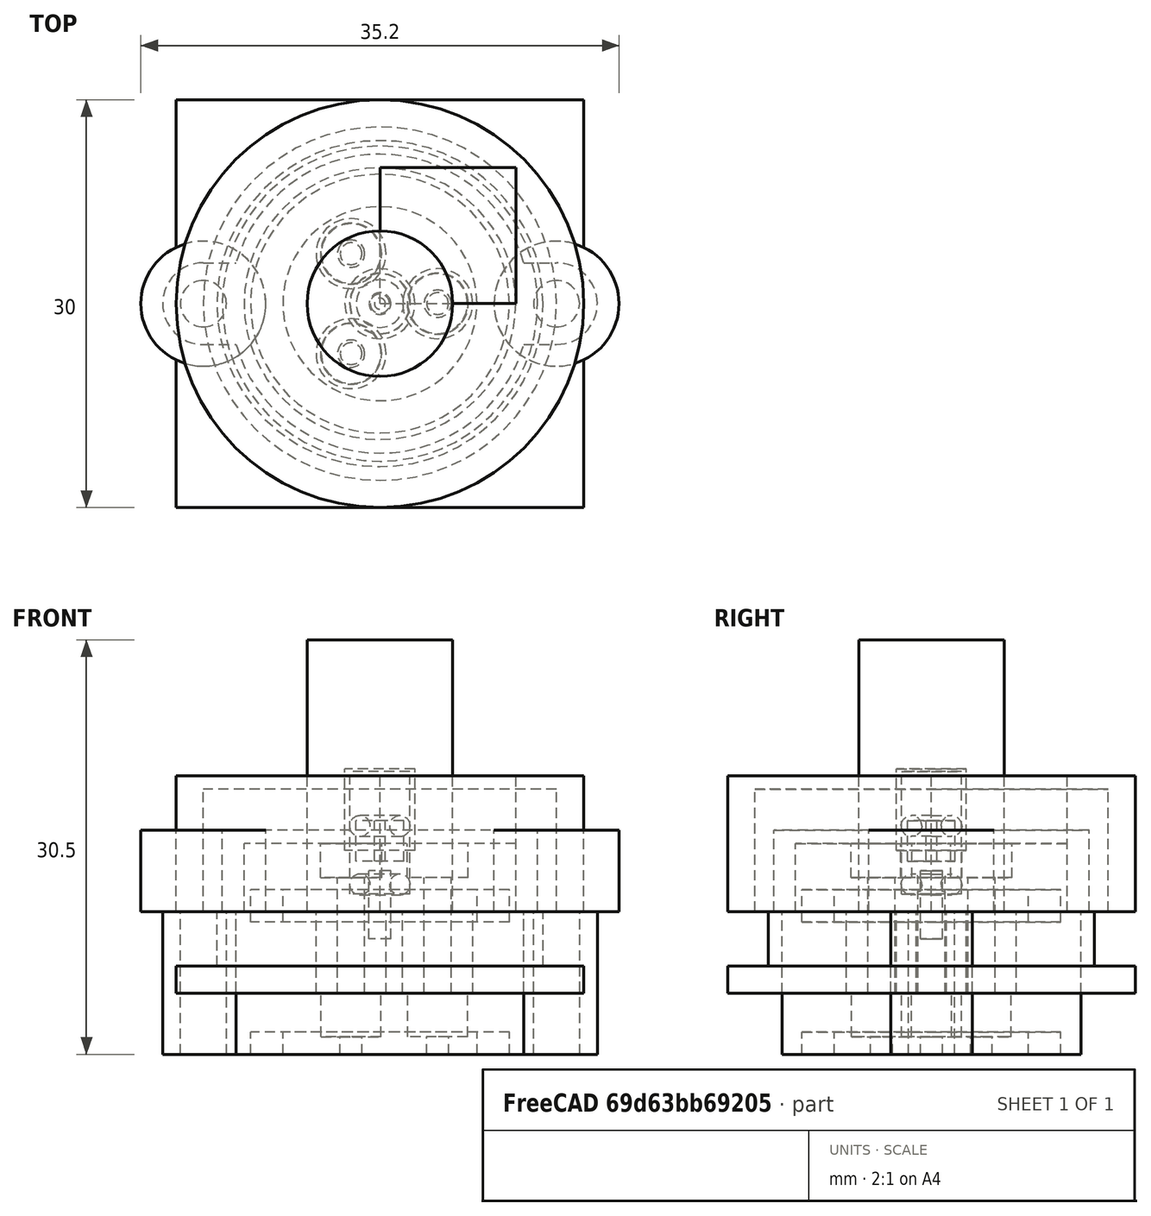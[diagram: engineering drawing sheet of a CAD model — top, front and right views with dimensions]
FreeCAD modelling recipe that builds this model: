
FCSTD DOCUMENT  (FreeCAD 0.17R13509 (Git))
Label: ceramic_wire_feedthroughs_insert_vertical
License: All rights reserved
LicenseURL: http://en.wikipedia.org/wiki/All_rights_reserved
objects: Part::Cylinder×48, Part::MultiFuse×11, Part::Cut×9, Part::Box×8, Part::FeaturePython×4, Part::Feature×2, App::FeaturePython×1
note: 82 computed .brp shape members not serialized (recipe doc carries the construction recipe); baked Part::Feature solids carry a one-line shape summary decoded from their .brp

FEATURE [Part::Cylinder] Cylinder155  label="Cylinder009"
  Angle = 360
  AttacherType = Attacher::AttachEngine3D
  Height = 2.38125
  Radius = 9.525
  expr: Radius = 3 / 4 * 25.399999999999999 / 2
  expr: Height = 3 / 32 * 25.399999999999999
FEATURE [Part::Cylinder] Cylinder154  label="Cylinder008"
  Angle = 360
  AttacherType = Attacher::AttachEngine3D
  Height = 2.38125
  Radius = 7.14375
  expr: Radius = 9 / 16 * 25.399999999999999 / 2
  expr: Height = 3 / 32 * 25.399999999999999
FEATURE [Part::Feature] Part__Feature001  label="TopOring"
  Placement = pos=(0,0,6.3) rot=(0,0,1;0rad)
  shape: bbox 4.839 x 4.839 x 1.524 mm, 4 faces (baked)
FEATURE [Part::Feature] Part__Feature002  label="BottomOring"
  Placement = pos=(0,0,2) rot=(0,0,1;0rad)
  shape: bbox 4.839 x 4.839 x 1.524 mm, 4 faces (baked)
FEATURE [Part::Cylinder] Cylinder153  label="Body"
  Angle = 360
  AttacherType = Attacher::AttachEngine3D
  Height = 5
  Radius = 10
FEATURE [Part::Cut] Cut019  label="Oring"
  Base = -> Cylinder155
  Placement = pos=(0,0,-0.75) rot=(0,0,1;0rad)
  Tool = -> Cylinder154
FEATURE [Part::Cylinder] Cylinder147  label="ThreadedSection"
  Angle = 360
  AttacherType = Attacher::AttachEngine3D
  Height = 1
  Placement = pos=(0,0,4.5) rot=(0,0,1;0rad)
  Radius = 1
FEATURE [Part::Cylinder] Cylinder149  label="FTBead"
  Angle = 360
  AttacherType = Attacher::AttachEngine3D
  Height = 3
  Placement = pos=(0,0,2.7) rot=(0,0,1;0rad)
  Radius = 1.75
  expr: Radius = 3.5 / 2
FEATURE [Part::Cylinder] Cylinder152  label="RFFeeds005"
  Angle = 360
  AttacherType = Attacher::AttachEngine3D
  Height = 20
  Radius = 5.35813
  expr: Placement.Base.x = 0
FEATURE [Part::Cylinder] Cylinder156  label="BottomWireOutlet"
  Angle = 360
  AttacherType = Attacher::AttachEngine3D
  Height = 18
  Placement = pos=(0,0,-8) rot=(0,0,1;0rad)
  Radius = 1
FEATURE [Part::Cylinder] Cylinder157  label="SealSubtraction"
  Angle = 360
  AttacherType = Attacher::AttachEngine3D
  Height = 8
  Placement = pos=(0,0,2.5) rot=(0,0,1;0rad)
  Radius = 2.25
FEATURE [Part::MultiFuse] Fusion
  Placement = pos=(4.25,0,0) rot=(0,0,1;0rad)
  Shapes = -> [Cylinder147,Cylinder157,Cylinder156]
FEATURE [Part::FeaturePython] Array  label="SealArray"  # Draft array (typed FeaturePython)
  Angle = 360
  ArrayType = 1
  Axis = (0,0,1)
  Base = -> Fusion
  Center = (0,0,0)
  Fuse = false
  IntervalAxis = (0,0,0)
  IntervalX = (1,0,0)
  IntervalY = (0,1,0)
  IntervalZ = (0,0,0)
  NumberPolar = 3
  NumberX = 2
  NumberY = 2
  NumberZ = 1
FEATURE [Part::Cylinder] Cylinder159  label="FTBeadHole"
  Angle = 360
  AttacherType = Attacher::AttachEngine3D
  Height = 17
  Radius = 0.405
  expr: Radius = 0.81000000000000005 / 2
FEATURE [Part::Cut] Cut020
  Base = -> Cylinder149
  Placement = pos=(0,0,1) rot=(0,0,1;0rad)
  Tool = -> Cylinder159
FEATURE [Part::Cylinder] Cylinder160  label="Cylinder010"
  Angle = 360
  AttacherType = Attacher::AttachEngine3D
  Height = 2.38125
  Radius = 9.525
  expr: Radius = 3 / 4 * 25.399999999999999 / 2
  expr: Height = 3 / 32 * 25.399999999999999
FEATURE [Part::Cylinder] Cylinder161  label="WireFeedsMount003"
  Angle = 360
  AttacherType = Attacher::AttachEngine3D
  Height = 11
  Placement = pos=(-13,0,0) rot=(0,0,1;0rad)
  Radius = 1.7
FEATURE [Part::Cylinder] Cylinder162  label="ThreadedSection001"
  Angle = 360
  AttacherType = Attacher::AttachEngine3D
  Height = 6
  Placement = pos=(0,0,4.5) rot=(0,0,1;0rad)
  Radius = 2.575
  expr: Radius = 5.1500000000000004 / 2
FEATURE [Part::Cylinder] Cylinder163  label="Cylinder011"
  Angle = 360
  AttacherType = Attacher::AttachEngine3D
  Height = 2.38125
  Radius = 7.14375
  expr: Radius = 9 / 16 * 25.399999999999999 / 2
  expr: Height = 3 / 32 * 25.399999999999999
FEATURE [Part::Cut] Cut022  label="Oring001"
  Base = -> Cylinder160
  Placement = pos=(0,0,-0.75) rot=(0,0,1;0rad)
  Tool = -> Cylinder163
FEATURE [Part::Cylinder] Cylinder164  label="Body001"
  Angle = 360
  AttacherType = Attacher::AttachEngine3D
  Height = 10.5
  Radius = 11
FEATURE [Part::Cylinder] Cylinder165  label="WireFeedsMount004"
  Angle = 360
  AttacherType = Attacher::AttachEngine3D
  Height = 11
  Placement = pos=(13,0,0) rot=(0,0,1;0rad)
  Radius = 1.7
FEATURE [Part::Cylinder] Cylinder166  label="BottomWireOutlet001"
  Angle = 360
  AttacherType = Attacher::AttachEngine3D
  Height = 5
  Placement = pos=(0,0,-2) rot=(0,0,1;0rad)
  Radius = 0.8
FEATURE [Part::Cylinder] Cylinder167  label="SealSubtraction001"
  Angle = 360
  AttacherType = Attacher::AttachEngine3D
  Height = 9
  Placement = pos=(0,0,1.3) rot=(0,0,1;0rad)
  Radius = 2.2
FEATURE [Part::Box] Box002  label="MountCube003"
  AttacherType = Attacher::AttachEngine3D
  Height = 10.5
  Length = 3
  Placement = pos=(10,-3,0) rot=(0,0,1;0rad)
  Width = 6
FEATURE [Part::Box] Box003  label="MountCube004"
  AttacherType = Attacher::AttachEngine3D
  Height = 10.5
  Length = 3
  Placement = pos=(-13,-3,0) rot=(0,0,1;0rad)
  Width = 6
FEATURE [Part::MultiFuse] Fusion004
  Placement = pos=(4.25,0,0) rot=(0,0,1;0rad)
  Shapes = -> [Cylinder162,Cylinder167,Cylinder166]
FEATURE [Part::Cylinder] Cylinder168  label="MountFlange003"
  Angle = 360
  AttacherType = Attacher::AttachEngine3D
  Height = 10.5
  Placement = pos=(-13,0,0) rot=(0,0,1;0rad)
  Radius = 3
FEATURE [Part::Cylinder] Cylinder169  label="MountFlange004"
  Angle = 360
  AttacherType = Attacher::AttachEngine3D
  Height = 10.5
  Placement = pos=(13,0,0) rot=(0,0,1;0rad)
  Radius = 3
FEATURE [Part::MultiFuse] Fusion003
  Shapes = -> [Cylinder169,Box002,Box003,Cylinder168,Cylinder164]
FEATURE [Part::FeaturePython] Array001  label="SealArray001"  # Draft array (typed FeaturePython)
  Angle = 360
  ArrayType = 1
  Axis = (0,0,1)
  Base = -> Fusion004
  Center = (0,0,0)
  Fuse = false
  IntervalAxis = (0,0,0)
  IntervalX = (1,0,0)
  IntervalY = (0,1,0)
  IntervalZ = (0,0,0)
  NumberPolar = 3
  NumberX = 2
  NumberY = 2
  NumberZ = 1
FEATURE [Part::MultiFuse] Fusion005
  Shapes = -> [Cylinder165,Cylinder161,Cut022,Array001]
FEATURE [Part::Cut] Cut021
  Base = -> Fusion003
  Placement = pos=(0,0,-10.5) rot=(0,0,1;0rad)
  Tool = -> Fusion005
FEATURE [Part::Cylinder] Cylinder170  label="Cylinder012"
  Angle = 360
  AttacherType = Attacher::AttachEngine3D
  Height = 2.38125
  Radius = 9.525
  expr: Radius = 3 / 4 * 25.399999999999999 / 2
  expr: Height = 3 / 32 * 25.399999999999999
FEATURE [Part::Cylinder] Cylinder171  label="WireFeedsMount005"
  Angle = 360
  AttacherType = Attacher::AttachEngine3D
  Height = 11
  Placement = pos=(-13,0,0) rot=(0,0,1;0rad)
  Radius = 1.7
FEATURE [Part::Cylinder] Cylinder172  label="ThreadedSection002"
  Angle = 360
  AttacherType = Attacher::AttachEngine3D
  Height = 6
  Placement = pos=(0,0,4.5) rot=(0,0,1;0rad)
  Radius = 2.575
  expr: Radius = 5.1500000000000004 / 2
FEATURE [Part::Cylinder] Cylinder173  label="Cylinder013"
  Angle = 360
  AttacherType = Attacher::AttachEngine3D
  Height = 2.38125
  Radius = 7.14375
  expr: Radius = 9 / 16 * 25.399999999999999 / 2
  expr: Height = 3 / 32 * 25.399999999999999
FEATURE [Part::Cut] Cut024  label="Oring002"
  Base = -> Cylinder170
  Placement = pos=(0,0,-0.75) rot=(0,0,1;0rad)
  Tool = -> Cylinder173
FEATURE [Part::Cylinder] Cylinder174  label="Body002"
  Angle = 360
  AttacherType = Attacher::AttachEngine3D
  Height = 10.5
  Radius = 11
FEATURE [Part::Cylinder] Cylinder175  label="WireFeedsMount006"
  Angle = 360
  AttacherType = Attacher::AttachEngine3D
  Height = 11
  Placement = pos=(13,0,0) rot=(0,0,1;0rad)
  Radius = 1.7
FEATURE [Part::Cylinder] Cylinder176  label="BottomWireOutlet002"
  Angle = 360
  AttacherType = Attacher::AttachEngine3D
  Height = 5
  Placement = pos=(0,0,-2) rot=(0,0,1;0rad)
  Radius = 0.8
FEATURE [Part::Cylinder] Cylinder177  label="SealSubtraction002"
  Angle = 360
  AttacherType = Attacher::AttachEngine3D
  Height = 9
  Placement = pos=(0,0,1.3) rot=(0,0,1;0rad)
  Radius = 2.2
FEATURE [Part::Box] Box004  label="MountCube005"
  AttacherType = Attacher::AttachEngine3D
  Height = 10.5
  Length = 3
  Placement = pos=(10,-3,0) rot=(0,0,1;0rad)
  Width = 6
FEATURE [App::FeaturePython] SetupSheet002  # Path/CAM operation (typed FeaturePython)
  ClearanceHeightExpression = StartDepth+SetupSheet.ClearanceHeightOffset
  ClearanceHeightOffset = 5
  FinalDepthExpression = OpFinalDepth
  HorizRapid = 0
  SafeHeightExpression = StartDepth+SetupSheet.SafeHeightOffset
  SafeHeightOffset = 3
  StartDepthExpression = OpStartDepth
  StepDownExpression = OpToolDiameter
  VertRapid = 0
FEATURE [Part::Box] Box005  label="MountCube006"
  AttacherType = Attacher::AttachEngine3D
  Height = 10.5
  Length = 3
  Placement = pos=(-13,-3,0) rot=(0,0,1;0rad)
  Width = 6
FEATURE [Part::MultiFuse] Fusion007
  Placement = pos=(4.25,0,0) rot=(0,0,1;0rad)
  Shapes = -> [Cylinder172,Cylinder177,Cylinder176]
FEATURE [Part::Cylinder] Cylinder178  label="MountFlange005"
  Angle = 360
  AttacherType = Attacher::AttachEngine3D
  Height = 10.5
  Placement = pos=(-13,0,0) rot=(0,0,1;0rad)
  Radius = 3
FEATURE [Part::Cylinder] Cylinder179  label="MountFlange006"
  Angle = 360
  AttacherType = Attacher::AttachEngine3D
  Height = 10.5
  Placement = pos=(13,0,0) rot=(0,0,1;0rad)
  Radius = 3
FEATURE [Part::MultiFuse] Fusion006
  Shapes = -> [Cylinder179,Box004,Box005,Cylinder178,Cylinder174]
FEATURE [Part::FeaturePython] Array002  label="SealArray002"  # Draft array (typed FeaturePython)
  Angle = 360
  ArrayType = 1
  Axis = (0,0,1)
  Base = -> Fusion007
  Center = (0,0,0)
  Fuse = false
  IntervalAxis = (0,0,0)
  IntervalX = (1,0,0)
  IntervalY = (0,1,0)
  IntervalZ = (0,0,0)
  NumberPolar = 3
  NumberX = 2
  NumberY = 2
  NumberZ = 1
FEATURE [Part::MultiFuse] Fusion008
  Shapes = -> [Cylinder175,Cylinder171,Cut024,Array002]
FEATURE [Part::Cut] Cut023
  Base = -> Fusion006
  Placement = pos=(0,0,-10.5) rot=(0,0,1;0rad)
  Tool = -> Fusion008
FEATURE [Part::Cylinder] Cylinder180  label="Cylinder014"
  Angle = 360
  AttacherType = Attacher::AttachEngine3D
  Height = 2.38125
  Radius = 7.14375
  expr: Radius = 9 / 16 * 25.399999999999999 / 2
  expr: Height = 3 / 32 * 25.399999999999999
FEATURE [Part::Cylinder] Cylinder181  label="MountFlange007"
  Angle = 360
  AttacherType = Attacher::AttachEngine3D
  Height = 10.5
  Placement = pos=(-13,0,0) rot=(0,0,1;0rad)
  Radius = 3
FEATURE [Part::Box] Box006  label="MountCube007"
  AttacherType = Attacher::AttachEngine3D
  Height = 10.5
  Length = 3
  Placement = pos=(-13,-3,0) rot=(0,0,1;0rad)
  Width = 6
FEATURE [Part::Cylinder] Cylinder182  label="WireFeedsMount007"
  Angle = 360
  AttacherType = Attacher::AttachEngine3D
  Height = 11
  Placement = pos=(13,0,0) rot=(0,0,1;0rad)
  Radius = 1.7
FEATURE [Part::Box] Box007  label="MountCube008"
  AttacherType = Attacher::AttachEngine3D
  Height = 10.5
  Length = 3
  Placement = pos=(10,-3,0) rot=(0,0,1;0rad)
  Width = 6
FEATURE [Part::Cylinder] Cylinder183  label="WireFeedsMount008"
  Angle = 360
  AttacherType = Attacher::AttachEngine3D
  Height = 11
  Placement = pos=(-13,0,0) rot=(0,0,1;0rad)
  Radius = 1.7
FEATURE [Part::Cylinder] Cylinder184  label="Body003"
  Angle = 360
  AttacherType = Attacher::AttachEngine3D
  Height = 10.5
  Radius = 11
FEATURE [Part::Cylinder] Cylinder185  label="MountFlange008"
  Angle = 360
  AttacherType = Attacher::AttachEngine3D
  Height = 10.5
  Placement = pos=(13,0,0) rot=(0,0,1;0rad)
  Radius = 3
FEATURE [Part::Cylinder] Cylinder186  label="BottomWireOutlet003"
  Angle = 360
  AttacherType = Attacher::AttachEngine3D
  Height = 5
  Placement = pos=(0,0,-2) rot=(0,0,1;0rad)
  Radius = 0.8
FEATURE [Part::MultiFuse] Fusion011
  Shapes = -> [Cylinder185,Box007,Box006,Cylinder181,Cylinder184]
FEATURE [Part::Cylinder] Cylinder187  label="ThreadedSection003"
  Angle = 360
  AttacherType = Attacher::AttachEngine3D
  Height = 6
  Placement = pos=(0,0,4.5) rot=(0,0,1;0rad)
  Radius = 2.575
  expr: Radius = 5.1500000000000004 / 2
FEATURE [Part::Cylinder] Cylinder188  label="Cylinder015"
  Angle = 360
  AttacherType = Attacher::AttachEngine3D
  Height = 2.38125
  Radius = 9.525
  expr: Radius = 3 / 4 * 25.399999999999999 / 2
  expr: Height = 3 / 32 * 25.399999999999999
FEATURE [Part::Cut] Cut025  label="Oring003"
  Base = -> Cylinder188
  Placement = pos=(0,0,-0.75) rot=(0,0,1;0rad)
  Tool = -> Cylinder180
FEATURE [Part::Cylinder] Cylinder189  label="SealSubtraction003"
  Angle = 360
  AttacherType = Attacher::AttachEngine3D
  Height = 9
  Placement = pos=(0,0,1.3) rot=(0,0,1;0rad)
  Radius = 2.2
FEATURE [Part::MultiFuse] Fusion009
  Placement = pos=(4.25,0,0) rot=(0,0,1;0rad)
  Shapes = -> [Cylinder187,Cylinder189,Cylinder186]
FEATURE [Part::FeaturePython] Array003  label="SealArray003"  # Draft array (typed FeaturePython)
  Angle = 360
  ArrayType = 1
  Axis = (0,0,1)
  Base = -> Fusion009
  Center = (0,0,0)
  Fuse = false
  IntervalAxis = (0,0,0)
  IntervalX = (1,0,0)
  IntervalY = (0,1,0)
  IntervalZ = (0,0,0)
  NumberPolar = 3
  NumberX = 2
  NumberY = 2
  NumberZ = 1
FEATURE [Part::MultiFuse] Fusion010
  Shapes = -> [Cylinder182,Cylinder183,Cut025,Array003]
FEATURE [Part::Cut] Cut026
  Base = -> Fusion011
  Placement = pos=(0,0,-10.5) rot=(0,0,1;0rad)
  Tool = -> Fusion010
FEATURE [Part::Cylinder] Cylinder192  label="ThreadedSection004"
  Angle = 360
  AttacherType = Attacher::AttachEngine3D
  Height = 6
  Placement = pos=(0,0,4.5) rot=(0,0,1;0rad)
  Radius = 2.575
  expr: Radius = 5.1500000000000004 / 2
FEATURE [Part::Cylinder] Cylinder196  label="BottomWireOutlet004"
  Angle = 360
  AttacherType = Attacher::AttachEngine3D
  Height = 5
  Placement = pos=(0,0,-2) rot=(0,0,1;0rad)
  Radius = 0.8
FEATURE [Part::Cylinder] Cylinder197  label="SealSubtraction004"
  Angle = 360
  AttacherType = Attacher::AttachEngine3D
  Height = 9
  Placement = pos=(0,0,1.3) rot=(0,0,1;0rad)
  Radius = 2.2
FEATURE [Part::Cylinder] Cylinder198  label="Cylinder"
  Angle = 360
  AttacherType = Attacher::AttachEngine3D
  Height = 6
  Radius = 11.6
FEATURE [Part::Cylinder] Cylinder199  label="Cylinder016"
  Angle = 360
  AttacherType = Attacher::AttachEngine3D
  Height = 6
  Placement = pos=(-13,0,0) rot=(0,0,1;0rad)
  Radius = 4.6
FEATURE [Part::Cylinder] Cylinder200  label="Cylinder017"
  Angle = 360
  AttacherType = Attacher::AttachEngine3D
  Height = 6
  Placement = pos=(13,0,0) rot=(0,0,1;0rad)
  Radius = 4.6
FEATURE [Part::Box] Box  label="Cube"
  AttacherType = Attacher::AttachEngine3D
  Height = 2
  Length = 30
  Placement = pos=(-15,-15,-6) rot=(0,0,1;0rad)
  Width = 30
FEATURE [Part::Cylinder] Cylinder  label="Cylinder018"
  Angle = 360
  AttacherType = Attacher::AttachEngine3D
  Height = 9
  Radius = 13
FEATURE [Part::Cylinder] Cylinder201  label="Cylinder019"
  Angle = 360
  AttacherType = Attacher::AttachEngine3D
  Height = 10
  Radius = 15
FEATURE [Part::Box] Box008  label="Cube001"
  AttacherType = Attacher::AttachEngine3D
  Height = 10
  Length = 10
  Width = 10
FEATURE [Part::Cylinder] Cylinder202  label="Cylinder020"
  Angle = 360
  AttacherType = Attacher::AttachEngine3D
  Height = 6
  Placement = pos=(0,0,-6) rot=(0,0,1;0rad)
  Radius = 12
FEATURE [Part::MultiFuse] Fusion012
  Shapes = -> [Cylinder202,Cylinder153,Box]
FEATURE [Part::Cut] Cut
  Base = -> Fusion012
  Tool = -> Array
